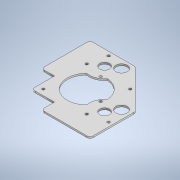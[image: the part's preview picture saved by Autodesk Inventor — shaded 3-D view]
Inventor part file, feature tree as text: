
AUTODESK INVENTOR PART (.ipt)
format: ipt  version: 2020 (Build 240168000, 168)  size: 301,568 bytes
history: native  units: in
note: dims shown in document units (in); Inventor stores cm internally (conversion verified against a paired STEP export)
features: extrude x4, sketch x4, hole x1, chamfer x1, fillet x1
ambient origin geometry x8: Origin, YZ Plane, XZ Plane, XY Plane, X Axis, Y Axis, Z Axis, Center Point
bodies: Solid1 (feature_tree)
feature tree (11):
  extrude  "Extrusion1"  Depth=0.125in TaperAngle=0.0deg
  hole  "Hole1"  [1 undecoded]
  sketch  "Sketch3"  dims[d5=4.25in d9=4.75in]
  extrude  "Extrusion5"  Depth=4.75in
  extrude  "Extrusion6"  Depth=0.25in
  extrude  "Extrusion7"  Depth=0.25in
  chamfer  "Chamfer3"  Distance=6.5in
  fillet  "Fillet6"  Radius=1.9in
  sketch  "Sketch1"  dims[d0=3.0in d1=0.125in d2=0.0in]
  sketch  "Sketch2"  dims[d3=1.0in d4=1.0in]
  sketch  "Sketch5"  dims[d10=0.196in d11=0.75in d12=0.5in d13=0.188in d14=0.5635in d15=1.0in d16=0.8108in d17=4.25in d19=0.75in d25=6.5in d33=1.9in d34=2.7272in d35=0.875in d37=2.0in d38=2.362in d39=0.375in d52=0.196in d53=90.0deg d56=90.0deg d59=0.0in d60=0.0in d61=1.0in d62=0.0in d63=1.0in d64=2.75in d65=1.75in d66=1.0in d67=1.0in d68=0.0in d73=3.0in d74=0.125in d75=45.0deg d76=0.25in]
note: 1 required parameter value undecoded (feature->parameter linkage not recoverable at this tier; creation-order binding heuristic only, values carry confidence <= 0.55)
